# Revit family: HD014-2016.01.12-BT-Conjunto Minitubrise
name_source: partatom
category: Generic Models
revit_build: Autodesk Revit 2016 (Build: 20150714_1515(x64)
units: mm (PartAtom-declared; Revit-internal decimal feet)

## family parameters
Always vertical = Yes
Can host rebar = No
Cut with Voids When Loaded = No
Part Type = Normal
Room Calculation Point = No
Round Connector Dimension = Use Diameter
Shared = No
Work Plane-Based = No

## types (1)
- Productos HD
    BT_Alto = d= 9 mm
    BT_Ancho = d= 9 mm
    BT_Codigo_Origen = HD018
    BT_Color = 100 colores a eleccion
    BT_Descripcion = Minitubrise Horizontal - Paso Minimo 20 mm
    BT_EETT = -
    BT_Elemento = Celosias y Quiebravista
    BT_Especialidad = Arquitectura
    BT_Fabricante = Hunter Douglas
    BT_Itemizado_Estandar_CDT = D 01 08 03
    BT_Linea = De Linea
    BT_Marca = Hunter Douglas
    BT_MasterFormat® = 08 91 19
    BT_Material = Aluzinc/ Aluminio
    BT_Nombre_Comercial = Minitubrise
    BT_Nombre_Corto = Minitubrise
    BT_Nombre_Tecnico = Minitubrise Horizontal
    BT_Profundidad = Largo Máximo 6 mts
    BT_SKU = 003617
    BT_Uso = Exterior
    BT_Web_del_Producto = http://www.hunterdouglas.cl
    Cantidad  Paneles = 83
    Cantidad apoyos = 3
    Description = Minitubrise Horizontal - Paso Minimo 20 mm
    Distancia  entre apoyos = 1000 mm  [stored 3.28084 ft]
    ID_Objeto = BT_F_F_018
    ID_Source = BIMTOOL
    Largo Panel (Editar Largo en tipo de panel) = 1200 mm
    Largo Portapanel = 1650 mm  [stored 5.41339 ft]
    Manufacturer = Hunter Douglas
    URL = http://www.hunterdouglas.cl
    paso = 20 mm  [stored 0.0656168 ft]

note: [stored X ft] marks values corroborated as IEEE doubles in the binary element streams (Revit-internal decimal feet)

## geometry (parser evidence)
native form markers: Sweep x13
no freeform markers — native parametric forms only
